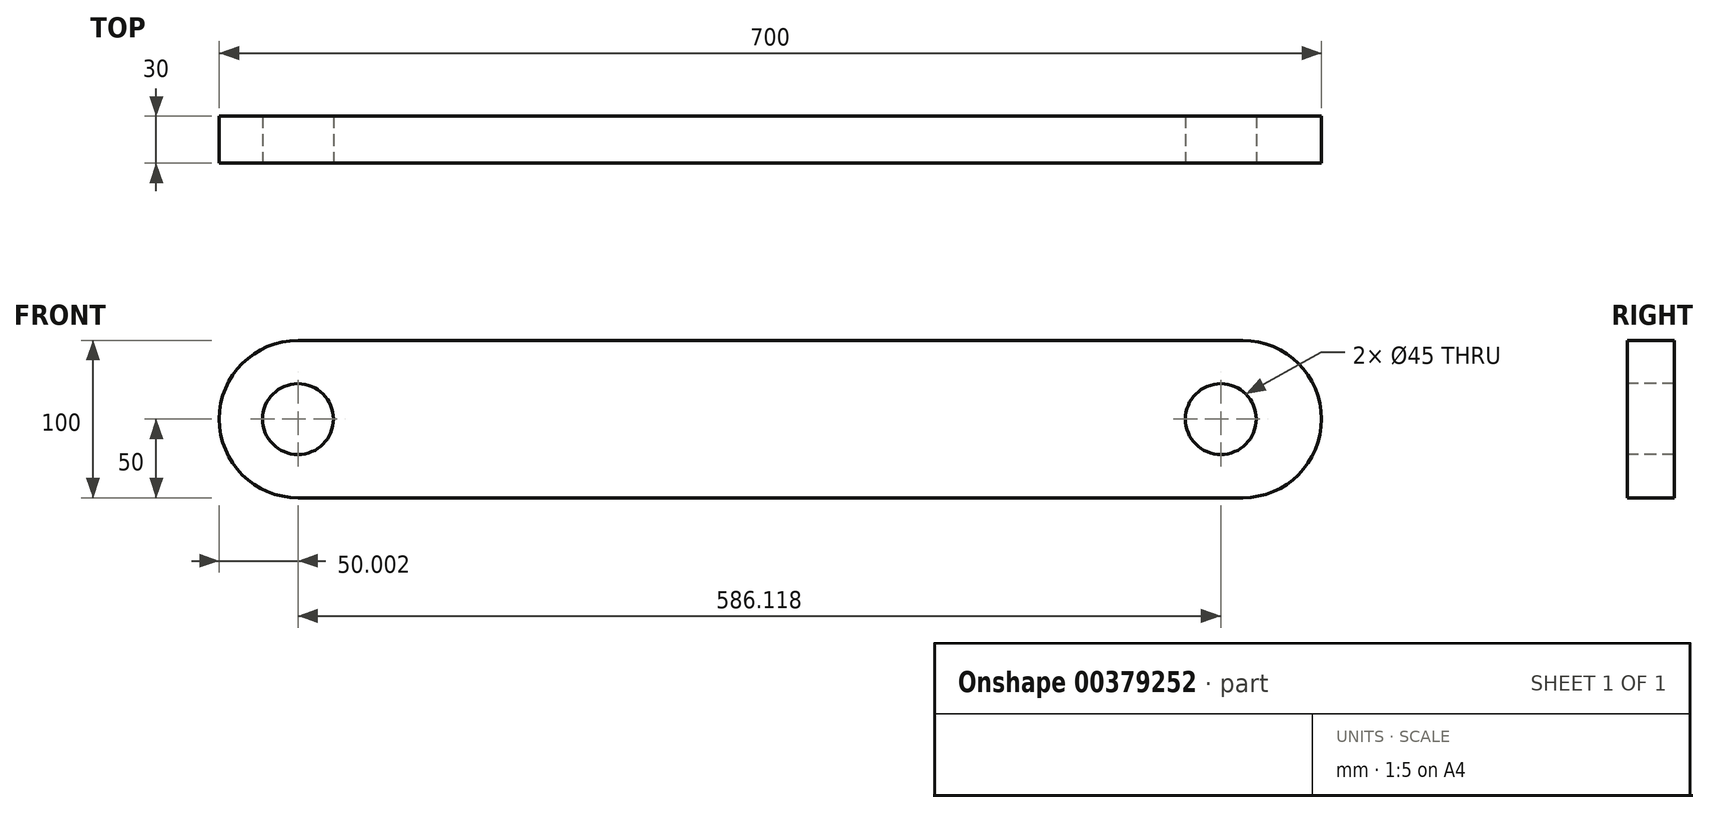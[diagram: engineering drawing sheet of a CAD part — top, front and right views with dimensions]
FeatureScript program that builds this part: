
annotation { "Feature Type Name" : "Feature", "Feature Type Description" : "" }
export const myFeature = defineFeature(function(context is Context, id is Id, definition is map)
    precondition{}
    {
        {
            var Q0;
            Q0=qCreatedBy(makeId("Front.planeOp"),FACE);
            var sketch = newSketch(context, id + "F0", { "sketchPlane" : qUnion([Q0])});
            skCircle(sketch, "E0", {"center": v(-586.12, 0) * mm, "radius": 50 * mm});
            skCircle(sketch, "E1", {"center": v(13.88, 0) * mm, "radius": 50 * mm});
            skLineSegment(sketch, "E2", {"start": v(-586.12, -50) * mm, "end": v(13.88, -50) * mm});
            skLineSegment(sketch, "E3", {"start": v(-586.12, 50) * mm, "end": v(13.88, 50) * mm});
            skSolve(sketch);
        }
        {
            var Q0;
            {var subQ0=sQuery(id+"F0.wireOp",EDGE,"E2");Q0=makeQuery(id+"F0.imprint","IMPRINT",FACE,{"disambiguationData":[TD([[makeQuery(id+"F0.imprint","IMPRINT",EDGE,{"derivedFrom":subQ0}),1.0]])]});}
            var Q1;
            {var subQ0=sQuery(id+"F0.wireOp",EDGE,"E1");var subQ1=makeQuery(id+"F0.imprint","INTERSECT",VERTEX,{"derivedFrom":[subQ0,sQuery(id+"F0.wireOp",EDGE,"E2")]});Q1=makeQuery(id+"F0.imprint","IMPRINT",FACE,{"disambiguationData":[TD([[makeQuery(id+"F0.imprint","IMPRINT",EDGE,{"disambiguationData":[TD([[subQ1,1.0]])],"derivedFrom":subQ0}),1.0]])]});}
            var Q2;
            {var subQ0=sQuery(id+"F0.wireOp",EDGE,"E0");var subQ1=makeQuery(id+"F0.imprint","INTERSECT",VERTEX,{"derivedFrom":[subQ0,sQuery(id+"F0.wireOp",EDGE,"E2")]});Q2=makeQuery(id+"F0.imprint","IMPRINT",FACE,{"disambiguationData":[TD([[makeQuery(id+"F0.imprint","IMPRINT",EDGE,{"disambiguationData":[TD([[subQ1,1.0]])],"derivedFrom":subQ0}),1.0]])]});}
            extrude(context, id + "F1", {"entities" : qUnion([Q0, Q1, Q2]), "depth" : 30 * mm});
        }
        {
            var Q0;
            Q0=makeQuery(id+"F1.opExtrude","CAP_FACE",FACE,{"disambiguationData":[OSD([sQuery(id+"F0.wireOp",EDGE,"E0"),sQuery(id+"F0.wireOp",EDGE,"E1"),sQuery(id+"F0.wireOp",EDGE,"E2"),sQuery(id+"F0.wireOp",EDGE,"E3")])],"isStart":false});
            var sketch = newSketch(context, id + "F2", { "sketchPlane" : qUnion([Q0])});
            skCircle(sketch, "E4", {"center": v(-586.12, 0) * mm, "radius": 22.5 * mm});
            skCircle(sketch, "E5", {"center": v(0, 0) * mm, "radius": 22.5 * mm});
            skSolve(sketch);
        }
        {
            var Q0;
            Q0=makeQuery(id+"F2.imprint","IMPRINT",FACE,{"disambiguationData":[TD([[makeQuery(id+"F2.imprint","IMPRINT",EDGE,{"derivedFrom":sQuery(id+"F2.wireOp",EDGE,"E4")}),1.0]])]});
            var Q1;
            Q1=makeQuery(id+"F2.imprint","IMPRINT",FACE,{"disambiguationData":[TD([[makeQuery(id+"F2.imprint","IMPRINT",EDGE,{"derivedFrom":sQuery(id+"F2.wireOp",EDGE,"E5")}),1.0]])]});
            extrude(context, id + "F3", {"entities" : qUnion([Q0, Q1]), "operationType" : NewBodyOperationType.REMOVE, "endBound" : BoundingType.UP_TO_NEXT, "oppositeDirection" : true, "depth" : 25 * mm});
        }
    });
